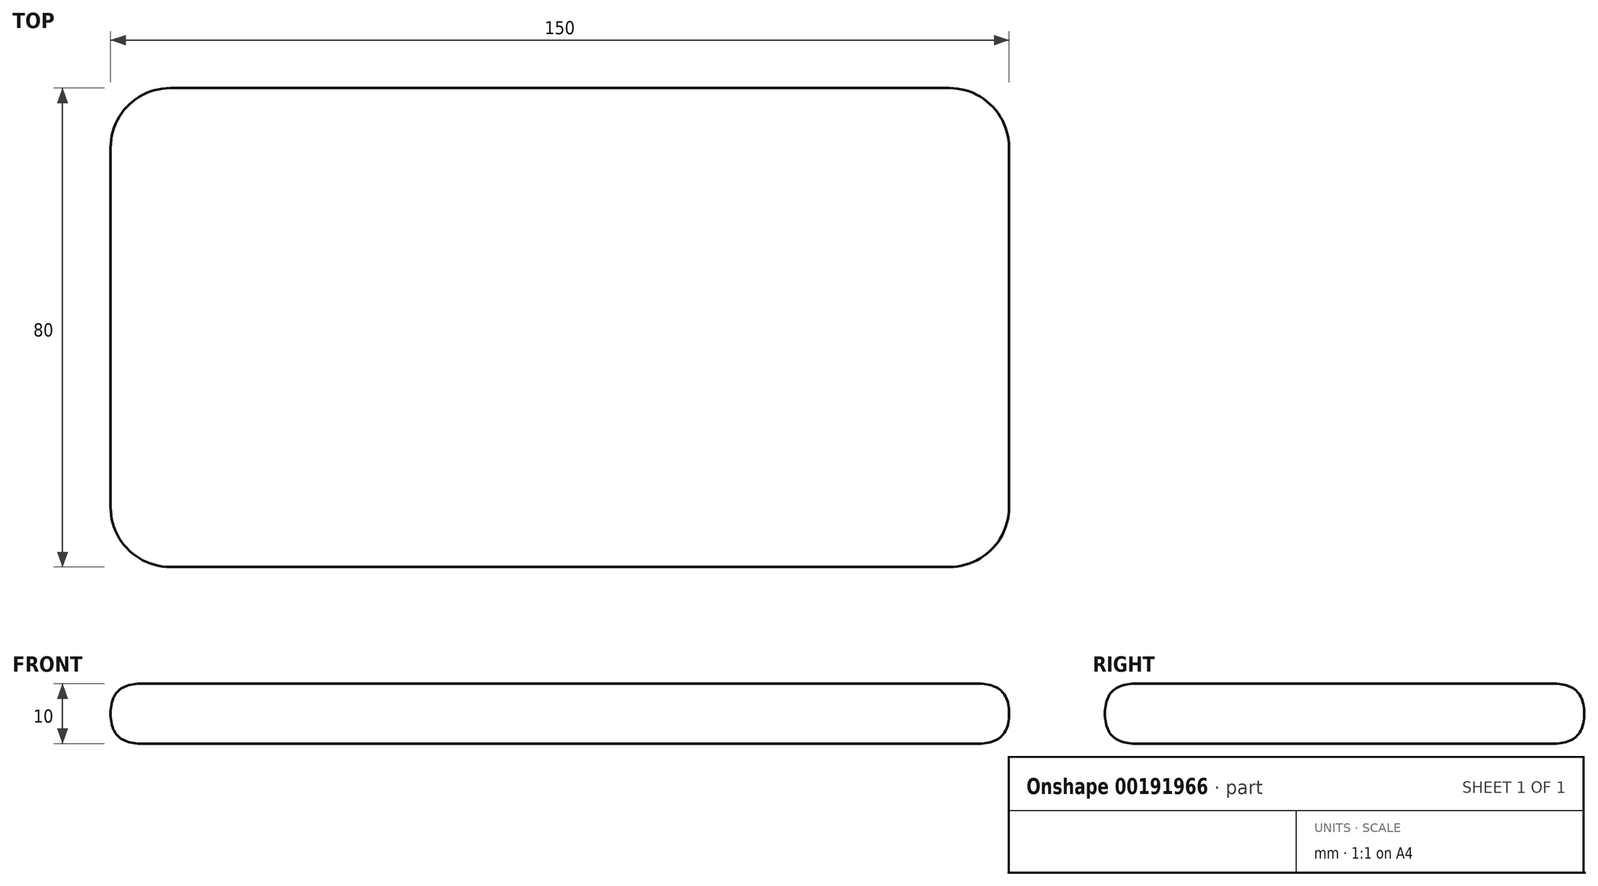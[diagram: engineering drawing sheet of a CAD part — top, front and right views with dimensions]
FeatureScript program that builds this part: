
annotation { "Feature Type Name" : "Feature", "Feature Type Description" : "" }
export const myFeature = defineFeature(function(context is Context, id is Id, definition is map)
    precondition{}
    {
        {
            var Q0;
            Q0=qCreatedBy(makeId("Top.planeOp"),FACE);
            var sketch = newSketch(context, id + "F0", { "sketchPlane" : qUnion([Q0])});
            skLineSegment(sketch, "E0.bottom", {"start": v(75, -40) * mm, "end": v(-75, -40) * mm});
            skLineSegment(sketch, "E0.top", {"start": v(75, 40) * mm, "end": v(-75, 40) * mm});
            skLineSegment(sketch, "E0.left", {"start": v(75, -40) * mm, "end": v(75, 40) * mm});
            skLineSegment(sketch, "E0.right", {"start": v(-75, -40) * mm, "end": v(-75, 40) * mm});
            skPoint(sketch, "E0.middle", {"position": v(0, 0) * mm});
            skSolve(sketch);
        }
        {
            var Q0;
            Q0=makeQuery(id+"F0.imprint","IMPRINT",FACE,{"disambiguationData":[TD([[makeQuery(id+"F0.imprint","IMPRINT",EDGE,{"derivedFrom":sQuery(id+"F0.wireOp",EDGE,"E0.bottom")}),-1.0]])]});
            extrude(context, id + "F1", {"entities" : qUnion([Q0]), "depth" : 10 * mm});
        }
        {
            var Q0;
            Q0=makeQuery(id+"F1.opExtrude","SWEPT_EDGE",EDGE,{"disambiguationData":[OSD([sQuery(id+"F0.wireOp",EDGE,"E0.bottom"),sQuery(id+"F0.wireOp",EDGE,"E0.left")])]});
            var Q1;
            Q1=makeQuery(id+"F1.opExtrude","SWEPT_EDGE",EDGE,{"disambiguationData":[OSD([sQuery(id+"F0.wireOp",EDGE,"E0.top"),sQuery(id+"F0.wireOp",EDGE,"E0.left")])]});
            var Q2;
            Q2=makeQuery(id+"F1.opExtrude","SWEPT_EDGE",EDGE,{"disambiguationData":[OSD([sQuery(id+"F0.wireOp",EDGE,"E0.bottom"),sQuery(id+"F0.wireOp",EDGE,"E0.right")])]});
            var Q3;
            Q3=makeQuery(id+"F1.opExtrude","SWEPT_EDGE",EDGE,{"disambiguationData":[OSD([sQuery(id+"F0.wireOp",EDGE,"E0.top"),sQuery(id+"F0.wireOp",EDGE,"E0.right")])]});
            fillet(context, id + "F2", {"entities" : qUnion([Q0, Q1, Q2, Q3]), "radius" : 10 * mm, "tangentPropagation" : true, "allowEdgeOverflow" : false});
        }
        {
            var Q0;
            Q0=makeQuery(id+"F1.opExtrude","CAP_EDGE",EDGE,{"disambiguationData":[OSD([sQuery(id+"F0.wireOp",EDGE,"E0.bottom")])],"isStart":false});
            var Q1;
            Q1=makeQuery(id+"F1.opExtrude","CAP_EDGE",EDGE,{"disambiguationData":[OSD([sQuery(id+"F0.wireOp",EDGE,"E0.bottom")])],"isStart":true});
            fillet(context, id + "F3", {"entities" : qUnion([Q0, Q1]), "radius" : 5 * mm, "tangentPropagation" : true, "rho" : 0.5, "crossSection" : FilletCrossSection.CONIC, "allowEdgeOverflow" : false});
        }
    });
